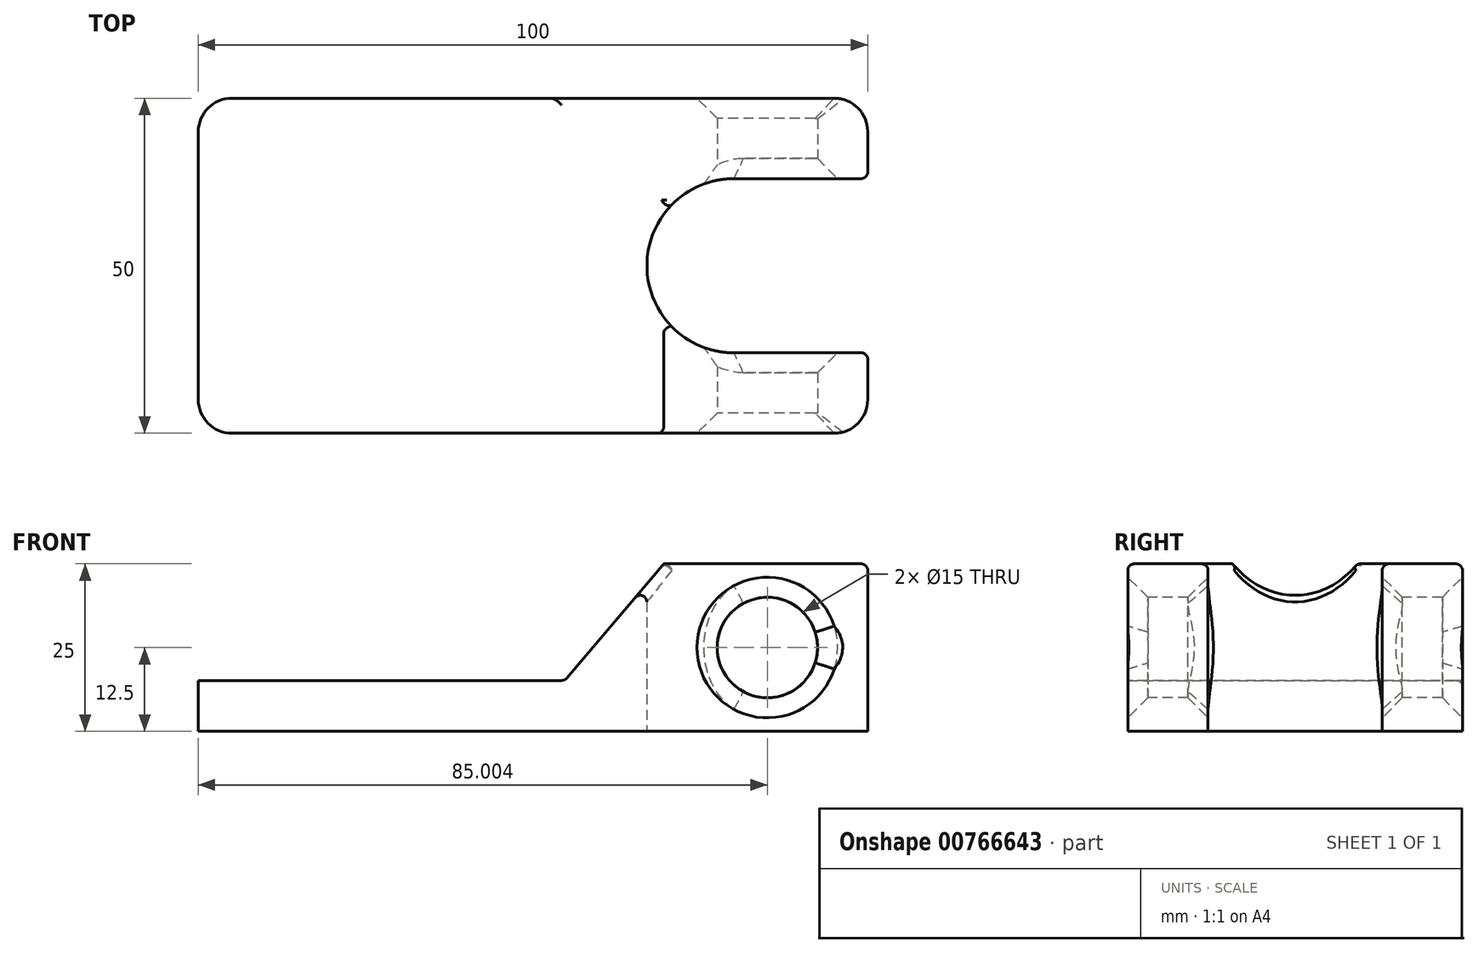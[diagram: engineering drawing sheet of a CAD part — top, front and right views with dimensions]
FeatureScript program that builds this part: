
annotation { "Feature Type Name" : "Feature", "Feature Type Description" : "" }
export const myFeature = defineFeature(function(context is Context, id is Id, definition is map)
    precondition{}
    {
        {
            var Q0;
            Q0=qCreatedBy(makeId("Top.planeOp"),FACE);
            var sketch = newSketch(context, id + "F0", { "sketchPlane" : qUnion([Q0])});
            skLineSegment(sketch, "E0.bottom", {"start": v(44, 8.41) * mm, "end": v(-46, 8.41) * mm});
            skLineSegment(sketch, "E0.top", {"start": v(44, -41.59) * mm, "end": v(-46, -41.59) * mm});
            skLineSegment(sketch, "E0.left", {"start": v(49, 3.41) * mm, "end": v(49, -36.59) * mm});
            skLineSegment(sketch, "E0.right", {"start": v(-51, 3.41) * mm, "end": v(-51, -36.59) * mm});
            skPoint(sketch, "E0.middle", {"position": v(-1, -16.59) * mm});
            skPoint(sketch, "E1.visualSharp", {"position": v(49, 8.41) * mm});
            skArc(sketch, "E1.filletArc", {"start": v(49, 3.41) * mm, "mid": v(47.53, 6.95) * mm, "end": v(44, 8.41) * mm});
            skPoint(sketch, "E2.visualSharp", {"position": v(49, -41.59) * mm});
            skArc(sketch, "E2.filletArc", {"start": v(44, -41.59) * mm, "mid": v(47.53, -40.12) * mm, "end": v(49, -36.59) * mm});
            skPoint(sketch, "E3.visualSharp", {"position": v(-51, -41.59) * mm});
            skArc(sketch, "E3.filletArc", {"start": v(-51, -36.59) * mm, "mid": v(-49.54, -40.12) * mm, "end": v(-46, -41.59) * mm});
            skPoint(sketch, "E4.visualSharp", {"position": v(-51, 8.41) * mm});
            skArc(sketch, "E4.filletArc", {"start": v(-46, 8.41) * mm, "mid": v(-49.54, 6.95) * mm, "end": v(-51, 3.41) * mm});
            skLineSegment(sketch, "E5", {"start": v(49, -3.59) * mm, "end": v(29, -3.59) * mm});
            skLineSegment(sketch, "E6", {"start": v(49, -29.59) * mm, "end": v(29, -29.59) * mm});
            skLineSegment(sketch, "E7", {"start": v(29, -29.59) * mm, "end": v(29, -3.59) * mm, "construction": true});
            skLineSegment(sketch, "E8", {"start": v(-1, -16.59) * mm, "end": v(49, -16.59) * mm, "construction": true});
            skPoint(sketch, "E8.endSnap0", {"position": v(29, -16.59) * mm});
            skArc(sketch, "E9", {"start": v(29, -29.59) * mm, "mid": v(16, -16.59) * mm, "end": v(29, -3.59) * mm});
            skSolve(sketch);
        }
        {
            var Q0;
            Q0=makeQuery(id+"F0.imprint","IMPRINT",FACE,{"disambiguationData":[TD([[makeQuery(id+"F0.imprint","IMPRINT",EDGE,{"derivedFrom":sQuery(id+"F0.wireOp",EDGE,"E0.bottom")}),1.0]])]});
            extrude(context, id + "F1", {"entities" : qUnion([Q0]), "depth" : 25 * mm, "offsetDistance" : 25 * mm});
        }
        {
            var Q0;
            Q0=makeQuery(id+"F1.opExtrude","SWEPT_FACE",FACE,{"disambiguationData":[OSD([sQuery(id+"F0.wireOp",EDGE,"E0.top")])]});
            var sketch = newSketch(context, id + "F2", { "sketchPlane" : qUnion([Q0])});
            skLineSegment(sketch, "E10", {"start": v(34, 0) * mm, "end": v(34, 12.5) * mm, "construction": true});
            skPoint(sketch, "E10.endSnap0", {"position": v(44, 12.5) * mm});
            skCircle(sketch, "E11", {"center": v(34, 12.5) * mm, "radius": 7.5 * mm});
            skLineSegment(sketch, "E12", {"start": v(-51.13, 7.59) * mm, "end": v(3.75, 7.59) * mm});
            skLineSegment(sketch, "E13", {"start": v(3.75, 7.59) * mm, "end": v(18.52, 25) * mm});
            skLineSegment(sketch, "E14", {"start": v(-51.13, 7.59) * mm, "end": v(-51.13, 25) * mm});
            skLineSegment(sketch, "E15", {"start": v(-51.13, 25) * mm, "end": v(18.52, 25) * mm});
            skSolve(sketch);
        }
        {
            var Q0;
            Q0=makeQuery(id+"F2.imprint","IMPRINT",FACE,{"disambiguationData":[TD([[makeQuery(id+"F2.imprint","IMPRINT",EDGE,{"derivedFrom":sQuery(id+"F2.wireOp",EDGE,"E11")}),1.0]])]});
            var Q1;
            Q1=sQuery(id+"F2.wireOp",EDGE,"E11");
            extrude(context, id + "F3", {"entities" : qUnion([Q0]), "operationType" : NewBodyOperationType.REMOVE, "surfaceEntities" : qUnion([Q1]), "endBound" : BoundingType.THROUGH_ALL, "oppositeDirection" : true, "depth" : 65.25 * mm, "offsetDistance" : 25 * mm});
        }
        {
            var Q0;
            Q0 = qSketchRegion(id + "F2", true);
            extrude(context, id + "F4", {"entities" : qUnion([Q0]), "operationType" : NewBodyOperationType.REMOVE, "endBound" : BoundingType.THROUGH_ALL, "oppositeDirection" : true, "depth" : 25 * mm, "offsetDistance" : 25 * mm});
        }
        {
            var Q0;
            Q0=makeQuery(id+"F4.boolean.opBoolean","INTERSECT",EDGE,{"derivedFrom":[makeQuery(id+"F1.opExtrude","SWEPT_FACE",FACE,{"disambiguationData":[OSD([sQuery(id+"F0.wireOp",EDGE,"E9")])]}),makeQuery(id+"F4.opExtrude","SWEPT_FACE",FACE,{"disambiguationData":[OSD([sQuery(id+"F2.wireOp",EDGE,"E13")])]})]});
            var Q1;
            Q1=makeQuery(id+"F1.opExtrude","CAP_EDGE",EDGE,{"disambiguationData":[OSD([sQuery(id+"F0.wireOp",EDGE,"E6")])],"isStart":false});
            var Q2;
            Q2=makeQuery(id+"F1.opExtrude","CAP_EDGE",EDGE,{"disambiguationData":[OSD([sQuery(id+"F0.wireOp",EDGE,"E5")])],"isStart":false});
            var Q3;
            {var subQ0=sQuery(id+"F0.wireOp",EDGE,"E0.bottom");var subQ2=sQuery(id+"F0.wireOp",EDGE,"E0.top");var subQ3=sQuery(id+"F2.wireOp",EDGE,"E13");Q3=makeQuery(id+"F4.boolean.opBoolean","COPY",EDGE,{"disambiguationData":[TD([makeQuery(id+"F1.opExtrude","SWEPT_FACE",FACE,{"disambiguationData":[OSD([subQ0])]})])],"derivedFrom":makeQuery(id+"F4.opExtrude","SWEPT_EDGE",EDGE,{"disambiguationData":[OSD([subQ2,subQ3,sQuery(id+"F2.wireOp",EDGE,"E15")])]})});}
            var Q4;
            {var subQ1=sQuery(id+"F0.wireOp",EDGE,"E0.top");var subQ2=sQuery(id+"F2.wireOp",EDGE,"E13");Q4=makeQuery(id+"F4.boolean.opBoolean","COPY",EDGE,{"disambiguationData":[TD([makeQuery(id+"F1.opExtrude","SWEPT_FACE",FACE,{"disambiguationData":[OSD([subQ1])]})])],"derivedFrom":makeQuery(id+"F4.opExtrude","SWEPT_EDGE",EDGE,{"disambiguationData":[OSD([subQ1,subQ2,sQuery(id+"F2.wireOp",EDGE,"E15")])]})});}
            var Q5;
            Q5=makeQuery(id+"F4.boolean.opBoolean","COPY",EDGE,{"derivedFrom":makeQuery(id+"F4.opExtrude","SWEPT_EDGE",EDGE,{"disambiguationData":[OSD([sQuery(id+"F2.wireOp",EDGE,"E12"),sQuery(id+"F2.wireOp",EDGE,"E13")])]})});
            var Q6;
            Q6=makeQuery(id+"F4.boolean.opBoolean","INTERSECT",EDGE,{"derivedFrom":[makeQuery(id+"F1.opExtrude","SWEPT_FACE",FACE,{"disambiguationData":[OSD([sQuery(id+"F0.wireOp",EDGE,"E0.bottom")])]}),makeQuery(id+"F4.opExtrude","SWEPT_FACE",FACE,{"disambiguationData":[OSD([sQuery(id+"F2.wireOp",EDGE,"E13")])]})]});
            var Q7;
            Q7=makeQuery(id+"F1.opExtrude","CAP_EDGE",EDGE,{"disambiguationData":[OSD([sQuery(id+"F0.wireOp",EDGE,"E0.bottom")])],"isStart":false});
            var Q8;
            Q8=makeQuery(id+"F1.opExtrude","CAP_EDGE",EDGE,{"disambiguationData":[OSD([sQuery(id+"F0.wireOp",EDGE,"E0.top")])],"isStart":false});
            var Q9;
            Q9=makeQuery(id+"F1.opExtrude","SWEPT_EDGE",EDGE,{"disambiguationData":[OSD([sQuery(id+"F0.wireOp",EDGE,"E0.left"),sQuery(id+"F0.wireOp",EDGE,"E5")])]});
            var Q10;
            Q10=makeQuery(id+"F1.opExtrude","SWEPT_EDGE",EDGE,{"disambiguationData":[OSD([sQuery(id+"F0.wireOp",EDGE,"E0.left"),sQuery(id+"F0.wireOp",EDGE,"E6")])]});
            fillet(context, id + "F5", {"entities" : qUnion([Q0, Q1, Q2, Q3, Q4, Q5, Q6, Q7, Q8, Q9, Q10]), "radius" : 1 * mm, "tangentPropagation" : true, "allowEdgeOverflow" : false});
        }
        {
            var Q0;
            Q0=makeQuery(id+"F3.boolean.opBoolean","COPY",FACE,{"disambiguationData":[TD([makeQuery(id+"F1.opExtrude","SWEPT_FACE",FACE,{"disambiguationData":[OSD([sQuery(id+"F0.wireOp",EDGE,"E0.top")])]})])],"derivedFrom":makeQuery(id+"F3.opExtrude","SWEPT_FACE",FACE,{"disambiguationData":[OSD([sQuery(id+"F2.wireOp",EDGE,"E11")])]})});
            var Q1;
            Q1=makeQuery(id+"F3.boolean.opBoolean","COPY",FACE,{"disambiguationData":[TD([makeQuery(id+"F1.opExtrude","SWEPT_FACE",FACE,{"disambiguationData":[OSD([sQuery(id+"F0.wireOp",EDGE,"E0.bottom")])]})])],"derivedFrom":makeQuery(id+"F3.opExtrude","SWEPT_FACE",FACE,{"disambiguationData":[OSD([sQuery(id+"F2.wireOp",EDGE,"E11")])]})});
            chamfer(context, id + "F6", {"entities" : qUnion([Q0, Q1]), "width" : 3 * mm, "tangentPropagation" : true});
        }
    });
